# Revit family: C_PPSDT160_2DO_CAD_MULT_Prod
name_source: partatom
category: Detail Items
revit_build: Autodesk Revit 2015 (Build: 20140606_1530(x64)
units: mm (PartAtom-declared; Revit-internal decimal feet)

## types (4) — shared parameters
Density = 0.77 kg
Description = Post bases
EPD = https://www.strongtie.eu
ETA / DoP = https://www.strongtie.eu
Manufacturer = Simpson Strong-Tie
Model = PPSDT160
Model Disclaimer = Contact Simpson Strong-Tie Company  for more information
Model ID = 0081687875147547144262547762410679911027
Name = PPSDT160
ObjectType = PPSDT160
Product Material = HotDipGalvanised
Product Type = Post bases
Reference = PPSDT160
Technical datasheet = https://www.strongtie.eu
URL = www.strongtie.eu
UniClass Number = Pr_20_29_31_45
UniClass Title = Joist hangers

## per-type parameters (varying)
| type | _visiblefront | _visibleleft | _visibleright | _visibletop |
| SST_PPSDT160_Front | Yes | No | No | No |
| SST_PPSDT160_Top | No | No | No | Yes |
| SST_PPSDT160_Left | No | Yes | No | No |
| SST_PPSDT160_Right | No | No | Yes | No |
